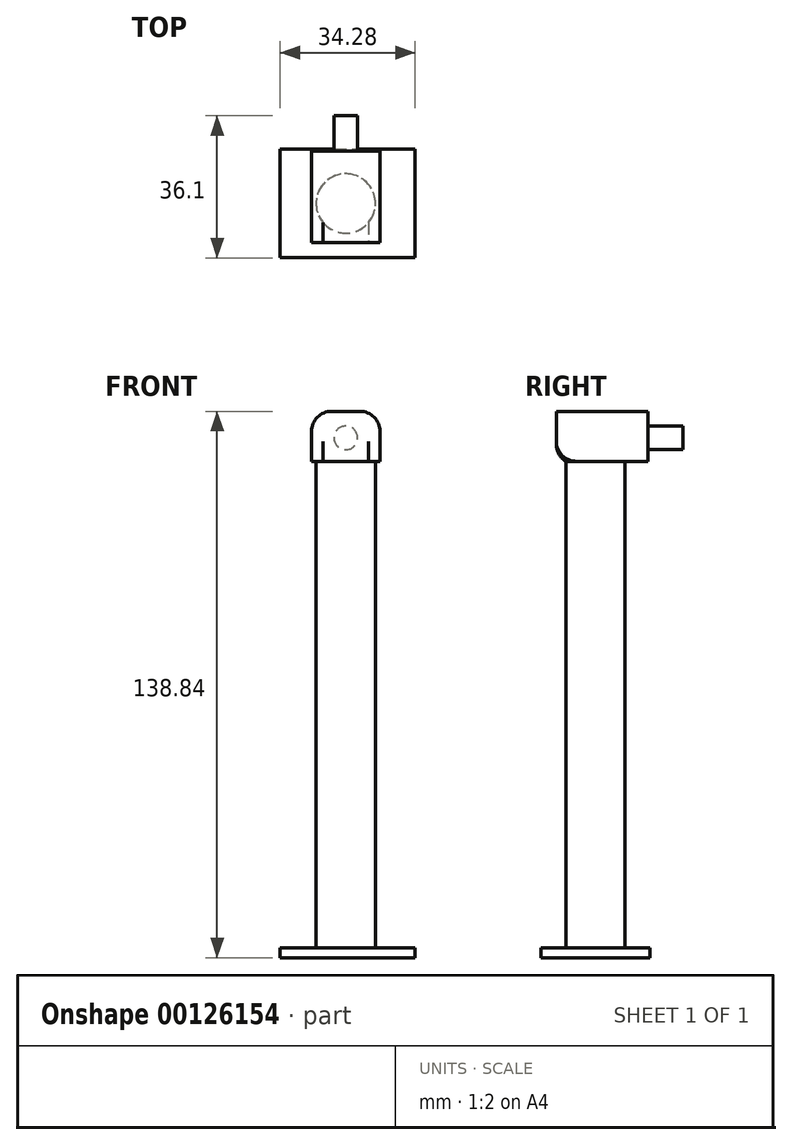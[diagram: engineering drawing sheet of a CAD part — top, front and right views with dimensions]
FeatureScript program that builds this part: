
annotation { "Feature Type Name" : "Feature", "Feature Type Description" : "" }
export const myFeature = defineFeature(function(context is Context, id is Id, definition is map)
    precondition{}
    {
        {
            var Q0;
            Q0=qCreatedBy(makeId("Top.planeOp"),FACE);
            var sketch = newSketch(context, id + "F0", { "sketchPlane" : qUnion([Q0])});
            skLineSegment(sketch, "E0.bottom", {"start": v(-16.65, -13.8) * mm, "end": v(17.63, -13.8) * mm});
            skLineSegment(sketch, "E0.top", {"start": v(-16.65, 13.8) * mm, "end": v(17.63, 13.8) * mm});
            skLineSegment(sketch, "E0.left", {"start": v(-16.65, -13.8) * mm, "end": v(-16.65, 13.8) * mm});
            skLineSegment(sketch, "E0.right", {"start": v(17.63, -13.8) * mm, "end": v(17.63, 13.8) * mm});
            skSolve(sketch);
        }
        {
            var Q0;
            Q0=makeQuery(id+"F0.imprint","IMPRINT",FACE,{"disambiguationData":[TD([[makeQuery(id+"F0.imprint","IMPRINT",EDGE,{"derivedFrom":sQuery(id+"F0.wireOp",EDGE,"E0.bottom")}),1.0]])]});
            extrude(context, id + "F1", {"entities" : qUnion([Q0]), "depth" : 2.47 * mm});
        }
        {
            var Q0;
            Q0=qCreatedBy(makeId("Top.planeOp"),FACE);
            var sketch = newSketch(context, id + "F2", { "sketchPlane" : qUnion([Q0])});
            skCircle(sketch, "E1", {"center": v(0, 0) * mm, "radius": 7.54 * mm});
            skSolve(sketch);
        }
        {
            var Q0;
            Q0 = qSketchRegion(id + "F2", true);
            extrude(context, id + "F3", {"entities" : qUnion([Q0]), "operationType" : NewBodyOperationType.ADD, "depth" : 126.15 * mm});
        }
        {
            var Q0;
            Q0=makeQuery(id+"F3.opExtrude","CAP_FACE",FACE,{"disambiguationData":[OSD([sQuery(id+"F2.wireOp",EDGE,"E1")])],"isStart":false});
            var sketch = newSketch(context, id + "F4", { "sketchPlane" : qUnion([Q0])});
            skLineSegment(sketch, "E2.bottom", {"start": v(-8.67, -9.95) * mm, "end": v(8.67, -9.95) * mm});
            skLineSegment(sketch, "E2.top", {"start": v(-8.67, 13.35) * mm, "end": v(8.67, 13.35) * mm});
            skLineSegment(sketch, "E2.left", {"start": v(-8.67, -9.95) * mm, "end": v(-8.67, 13.35) * mm});
            skLineSegment(sketch, "E2.right", {"start": v(8.67, -9.95) * mm, "end": v(8.67, 13.35) * mm});
            skSolve(sketch);
        }
        {
            var Q0;
            Q0 = qSketchRegion(id + "F4", true);
            extrude(context, id + "F5", {"entities" : qUnion([Q0]), "operationType" : NewBodyOperationType.ADD, "depth" : 12.7 * mm});
        }
        {
            var Q0;
            Q0=makeQuery(id+"F5.opExtrude","CAP_EDGE",EDGE,{"disambiguationData":[OSD([sQuery(id+"F4.wireOp",EDGE,"E2.left")])],"isStart":false});
            var Q1;
            Q1=makeQuery(id+"F5.opExtrude","CAP_EDGE",EDGE,{"disambiguationData":[OSD([sQuery(id+"F4.wireOp",EDGE,"E2.right")])],"isStart":false});
            fillet(context, id + "F6", {"entities" : qUnion([Q0, Q1]), "radius" : 5.08 * mm, "tangentPropagation" : true, "allowEdgeOverflow" : false});
        }
        {
            var Q0;
            Q0=makeQuery(id+"F5.opExtrude","CAP_EDGE",EDGE,{"disambiguationData":[OSD([sQuery(id+"F4.wireOp",EDGE,"E2.bottom")])],"isStart":true});
            fillet(context, id + "F7", {"entities" : qUnion([Q0]), "radius" : 5.08 * mm, "tangentPropagation" : true, "allowEdgeOverflow" : false});
        }
        {
            var Q0;
            Q0=makeQuery(id+"F5.opExtrude","SWEPT_FACE",FACE,{"disambiguationData":[OSD([sQuery(id+"F4.wireOp",EDGE,"E2.top")])]});
            var sketch = newSketch(context, id + "F8", { "sketchPlane" : qUnion([Q0])});
            skCircle(sketch, "E3", {"center": v(0, 132.09) * mm, "radius": 3 * mm});
            skSolve(sketch);
        }
        {
            var Q0;
            Q0=makeQuery(id+"F8.imprint","IMPRINT",FACE,{"disambiguationData":[TD([[makeQuery(id+"F8.imprint","IMPRINT",EDGE,{"derivedFrom":sQuery(id+"F8.wireOp",EDGE,"E3")}),1.0]])]});
            extrude(context, id + "F9", {"entities" : qUnion([Q0]), "operationType" : NewBodyOperationType.ADD, "depth" : 8.94 * mm});
        }
    });
